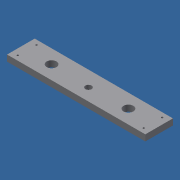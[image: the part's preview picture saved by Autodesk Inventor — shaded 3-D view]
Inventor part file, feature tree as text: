
AUTODESK INVENTOR PART (.ipt)
format: ipt  version: 2018 (Build 220112000, 112)  size: 102,400 bytes
history: native  units: mm
features: extrude x1, sketch x1
ambient origin geometry x8: Origin, YZ Plane, XZ Plane, XY Plane, X Axis, Y Axis, Z Axis, Center Point
bodies: Solid1 (feature_tree)
feature tree (2):
  extrude  "Extrusion1"  Depth=225.0mm
  sketch  "Sketch1"  dims[d0=45.0mm d1=225.0mm d2=30.0mm d3=3.0mm d4=3.0mm d5=7.5mm d6=7.5mm d7=3.0mm d8=3.0mm d9=30.0mm d10=10.0mm d11=10.0mm d12=10.0mm d13=0.0mm d14=16.0mm d15=16.0mm d16=22.5mm d17=22.5mm d18=50.0mm d19=50.0mm d20=10.2mm d21=25.0mm d22=112.5mm]
